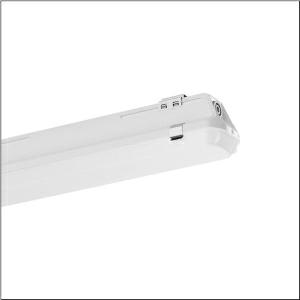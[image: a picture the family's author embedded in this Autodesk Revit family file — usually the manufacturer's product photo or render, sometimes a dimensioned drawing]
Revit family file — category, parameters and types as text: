
# Revit family: monsun_r__21_51fb107p460b005_4f74
name_source: partatom
category: Lighting Fixtures
units: mm (PartAtom-declared; Revit-internal decimal feet)

## family parameters
Cut with Voids When Loaded = No
Host = Face
Light Source = No
Part Type = Normal
Room Calculation Point = No
Round Connector Dimension = Use Diameter
Shared = No

## types (1)
- Monsun® 21 (1 x LED, 6000 lm, 38 W, 4000K)
    Apparent Load = 38 VA
    CIE Flux Codes = 47 77 93 94 100
    Color Rendering = 80
    Color Temperature = 4000K
    Default Elevation = 1800 mm
    Description = Monsun® 21, damp-proof luminaire, chain hanger, primary optical cover: enclosure, of PMMA, light emission: direct distribution, primary light characteristic: symmetric, installation type: suspended mounting, surface-mounted, horizontal mounting, vertical mounting, LED, rated luminous flux: 6.000lm, luminous efficacy: 158lm/W, light colour: 840, colour temperature: 4000K, control gear: ECG, with terminal, 3-pole, max. 2.5mm², through-wiring: 5x 2.5mm², mains connection: 220..240V, AC, 50/60Hz, rated input power: 38W, housing, of glass-fibre reinforced polyester, uncoated, bright grey, incl. chain hanger, length: 1.590mm, width: 90mm, height: 88mm, clip for enclosure, of stainless steel (V2A), ceiling mounting element, of stainless steel (V2A), chain hanger, of stainless steel (V2A), protection rating (complete): IP66, insulation class (complete): insulation class I (protective earthing), certification: CE, ENEC, VDE, UKCA, protection symbol: D, impact resistance: IK04, permissible operating ambient temperature: -25..+35°C, standard: EN 50419, EN 60598-2-1, corresponds to IFS (International Featured Standards) requirements for safety and quality in the food industry, for indoor or canopied outdoor use, no direct snow, no direct sun, no direct rain, contact your sales advisor before using the luminaires in applications with unclear chemical exposure, large temperature fluctuations or condensation-forming humidity, LABS conformity tested according to VDMA 24364:2018-05, packaging unit: 1 piece
    Height = 89 mm
    Lamp = 1 x LED
    Lamp Light Flux = 6000 lm
    Lamp Power = 38 W
    Lamp count = 1
    Length = 1590 mm
    Luminous efficacy = 158 lm/W
    Manufacturer = Siteco
    ModVariant = No
    Model = 51FB107P460B005
    Mounting Place = Ceiling
    Mounting Type = Surface mounted
    Number of Poles = 1
    OnlyDefault = Yes
    Power Factor = 1
    Product Name = Monsun® 21
    Product group = damp-proof luminaire
    ProductGroupID = 301
    Protection Class = Protection class I
    Protection Degree = IP 66
    RLX_Detail_Level = 1
    RLX_Emergency_Light_Flux = 0 lm
    RLX_Emergency_Type = 0
    RLX_Emergency_Type_DB = No
    RlxData = <blob elided: 88525 chars, md5=8b11ad65>
    Socket = socket
    Standby Power = 0 W
    System Light Flux = 6000 lm
    System Power = 38 W
    Type Comments = Product without accessories
    Type Image = l_1006717.jpg
    URL = http://relux.com
    VarID = ---
    Voltage = 0 V
    Weight = 0.00 kg
    Width = 90 mm

## geometry (parser evidence)
native form markers: Blend x4, Sweep x14
no freeform markers — native parametric forms only
